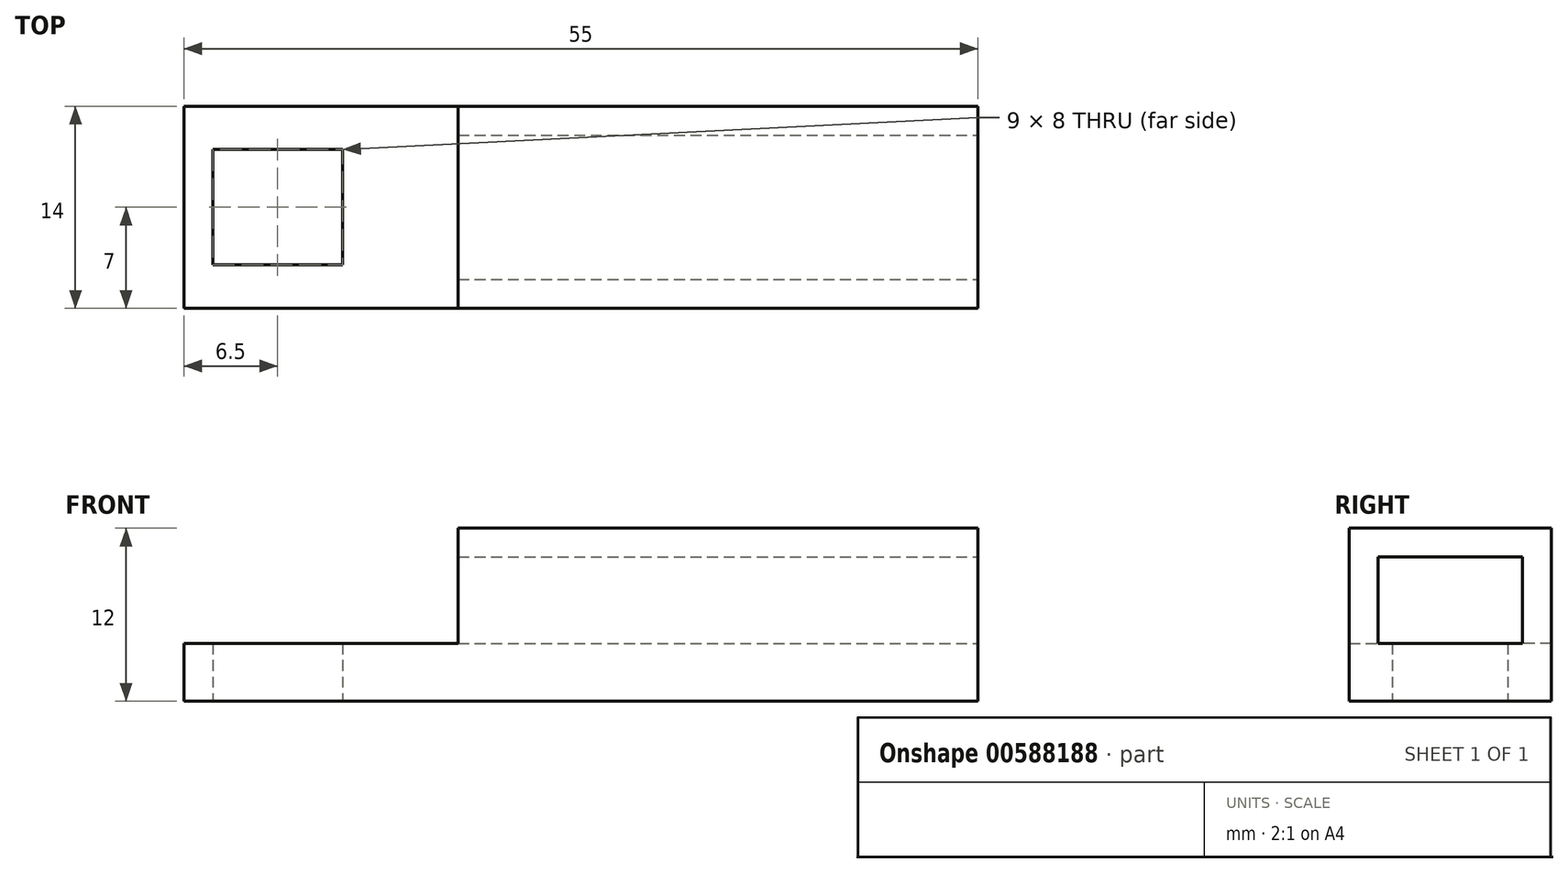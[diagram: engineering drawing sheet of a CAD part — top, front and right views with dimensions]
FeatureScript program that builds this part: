
annotation { "Feature Type Name" : "Feature", "Feature Type Description" : "" }
export const myFeature = defineFeature(function(context is Context, id is Id, definition is map)
    precondition{}
    {
        {
            var Q0;
            Q0=qCreatedBy(makeId("Top.planeOp"),FACE);
            var sketch = newSketch(context, id + "F0", { "sketchPlane" : qUnion([Q0])});
            skLineSegment(sketch, "E0.bottom", {"start": v(-27.5, 7) * mm, "end": v(27.5, 7) * mm});
            skLineSegment(sketch, "E0.top", {"start": v(-27.5, -7) * mm, "end": v(27.5, -7) * mm});
            skLineSegment(sketch, "E0.left", {"start": v(-27.5, 7) * mm, "end": v(-27.5, -7) * mm});
            skLineSegment(sketch, "E0.right", {"start": v(27.5, 7) * mm, "end": v(27.5, -7) * mm});
            skLineSegment(sketch, "E1", {"start": v(0, 7) * mm, "end": v(0, 0) * mm, "construction": true});
            skLineSegment(sketch, "E2", {"start": v(0, 0) * mm, "end": v(0, -7) * mm, "construction": true});
            skLineSegment(sketch, "E3", {"start": v(-27.5, 0) * mm, "end": v(0, 0) * mm, "construction": true});
            skLineSegment(sketch, "E4", {"start": v(27.5, 0) * mm, "end": v(0, 0) * mm, "construction": true});
            skLineSegment(sketch, "E5.bottom", {"start": v(-25.5, 4) * mm, "end": v(-16.5, 4) * mm});
            skLineSegment(sketch, "E5.top", {"start": v(-25.5, -4) * mm, "end": v(-16.5, -4) * mm});
            skLineSegment(sketch, "E5.left", {"start": v(-25.5, 4) * mm, "end": v(-25.5, -4) * mm});
            skLineSegment(sketch, "E5.right", {"start": v(-16.5, 4) * mm, "end": v(-16.5, 0) * mm});
            skLineSegment(sketch, "E6", {"start": v(-16.5, 0) * mm, "end": v(-16.5, -4) * mm});
            skSolve(sketch);
        }
        {
            var Q0;
            Q0=makeQuery(id+"F0.imprint","IMPRINT",FACE,{"disambiguationData":[TD([[makeQuery(id+"F0.imprint","IMPRINT",EDGE,{"derivedFrom":sQuery(id+"F0.wireOp",EDGE,"E0.bottom")}),-1.0]])]});
            extrude(context, id + "F1", {"entities" : qUnion([Q0]), "depth" : 4 * mm, "offsetDistance" : 25 * mm});
        }
        {
            var Q0;
            Q0=makeQuery(id+"F1.opExtrude","CAP_FACE",FACE,{"disambiguationData":[OSD([sQuery(id+"F0.wireOp",EDGE,"E0.bottom"),sQuery(id+"F0.wireOp",EDGE,"E0.top"),sQuery(id+"F0.wireOp",EDGE,"E0.left"),sQuery(id+"F0.wireOp",EDGE,"E0.right"),sQuery(id+"F0.wireOp",EDGE,"E5.bottom"),sQuery(id+"F0.wireOp",EDGE,"E5.top"),sQuery(id+"F0.wireOp",EDGE,"E5.left"),sQuery(id+"F0.wireOp",EDGE,"E5.right"),sQuery(id+"F0.wireOp",EDGE,"E6")])],"isStart":false});
            var sketch = newSketch(context, id + "F2", { "sketchPlane" : qUnion([Q0])});
            skLineSegment(sketch, "E7", {"start": v(-8.5, 7) * mm, "end": v(-8.5, -7) * mm, "construction": true});
            skLineSegment(sketch, "E8.bottom", {"start": v(-8.5, 7) * mm, "end": v(27.5, 7) * mm});
            skLineSegment(sketch, "E8.top", {"start": v(-8.5, 5) * mm, "end": v(27.5, 5) * mm});
            skLineSegment(sketch, "E8.left", {"start": v(-8.5, 7) * mm, "end": v(-8.5, 5) * mm});
            skLineSegment(sketch, "E8.right", {"start": v(27.5, 7) * mm, "end": v(27.5, 5) * mm});
            skLineSegment(sketch, "E9.bottom", {"start": v(-8.5, -7) * mm, "end": v(27.5, -7) * mm});
            skLineSegment(sketch, "E9.top", {"start": v(-8.5, -5) * mm, "end": v(27.5, -5) * mm});
            skLineSegment(sketch, "E9.left", {"start": v(-8.5, -7) * mm, "end": v(-8.5, -5) * mm});
            skLineSegment(sketch, "E9.right", {"start": v(27.5, -7) * mm, "end": v(27.5, -5) * mm});
            skSolve(sketch);
        }
        {
            var Q0;
            Q0=makeQuery(id+"F2.imprint","IMPRINT",FACE,{"disambiguationData":[TD([[makeQuery(id+"F2.imprint","IMPRINT",EDGE,{"derivedFrom":sQuery(id+"F2.wireOp",EDGE,"E9.bottom")}),1.0]])]});
            var Q1;
            Q1=makeQuery(id+"F2.imprint","IMPRINT",FACE,{"disambiguationData":[TD([[makeQuery(id+"F2.imprint","IMPRINT",EDGE,{"derivedFrom":sQuery(id+"F2.wireOp",EDGE,"E8.bottom")}),-1.0]])]});
            extrude(context, id + "F3", {"entities" : qUnion([Q0, Q1]), "operationType" : NewBodyOperationType.ADD, "depth" : 6 * mm, "offsetDistance" : 25 * mm});
        }
        {
            var Q0;
            Q0=makeQuery(id+"F3.opExtrude","CAP_FACE",FACE,{"disambiguationData":[OSD([sQuery(id+"F2.wireOp",EDGE,"E8.bottom"),sQuery(id+"F2.wireOp",EDGE,"E8.top"),sQuery(id+"F2.wireOp",EDGE,"E8.left"),sQuery(id+"F2.wireOp",EDGE,"E8.right")])],"isStart":false});
            var sketch = newSketch(context, id + "F4", { "sketchPlane" : qUnion([Q0])});
            skLineSegment(sketch, "E10.bottom", {"start": v(-8.5, 7) * mm, "end": v(27.5, 7) * mm});
            skLineSegment(sketch, "E10.top", {"start": v(-8.5, -7) * mm, "end": v(27.5, -7) * mm});
            skLineSegment(sketch, "E10.left", {"start": v(-8.5, 7) * mm, "end": v(-8.5, -7) * mm});
            skLineSegment(sketch, "E10.right", {"start": v(27.5, 7) * mm, "end": v(27.5, -7) * mm});
            skSolve(sketch);
        }
        {
            var Q0;
            Q0 = qSketchRegion(id + "F4", true);
            extrude(context, id + "F5", {"entities" : qUnion([Q0]), "operationType" : NewBodyOperationType.ADD, "depth" : 2 * mm, "offsetDistance" : 25 * mm});
        }
    });
